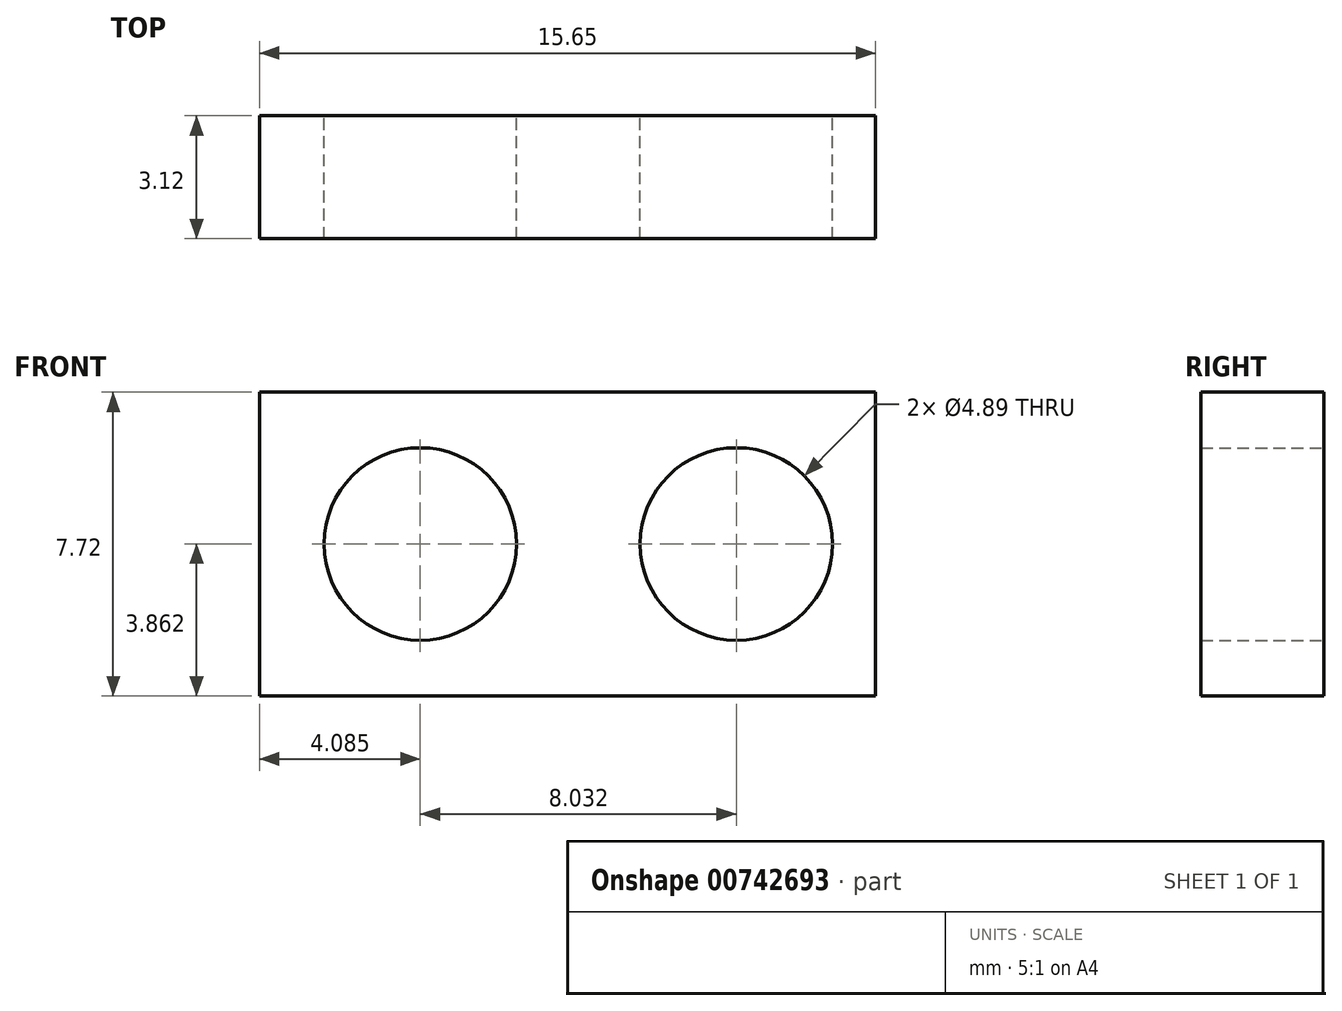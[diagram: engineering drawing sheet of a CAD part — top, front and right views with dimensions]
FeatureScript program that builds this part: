
annotation { "Feature Type Name" : "Feature", "Feature Type Description" : "" }
export const myFeature = defineFeature(function(context is Context, id is Id, definition is map)
    precondition{}
    {
        {
            var Q0;
            Q0=qCreatedBy(makeId("Front.planeOp"),FACE);
            var sketch = newSketch(context, id + "F0", { "sketchPlane" : qUnion([Q0])});
            skLineSegment(sketch, "E0", {"start": v(16.47, 32.45) * mm, "end": v(16.47, 24.73) * mm});
            skLineSegment(sketch, "E1", {"start": v(16.47, 24.73) * mm, "end": v(0.82, 24.73) * mm});
            skLineSegment(sketch, "E2", {"start": v(0.82, 24.73) * mm, "end": v(0.82, 32.45) * mm});
            skLineSegment(sketch, "E3", {"start": v(0.82, 32.45) * mm, "end": v(16.47, 32.45) * mm});
            skCircle(sketch, "E4", {"center": v(4.9, 28.6) * mm, "radius": 2.44 * mm});
            skCircle(sketch, "E5", {"center": v(12.94, 28.6) * mm, "radius": 2.44 * mm});
            skPoint(sketch, "E6.orphan", {"position": v(0.82, 28.59) * mm});
            skPoint(sketch, "E7.end.orphan", {"position": v(4.9, 28.59) * mm});
            skPoint(sketch, "E8.start.orphan", {"position": v(16.47, 28.59) * mm});
            skSolve(sketch);
        }
        {
            var Q0;
            Q0 = qSketchRegion(id + "F0", true);
            extrude(context, id + "F1", {"entities" : qUnion([Q0]), "depth" : 3.12 * mm, "offsetDistance" : 25 * mm});
        }
    });
